# Revit family: Domotics-DomesticRanges-GEWISS-CHORUS_POWER-SOCKET-OUTLET_13A_ENG
name_source: partatom
category: Apparecchi elettrici
revit_build: Autodesk Revit 2016 (Build: 20161004_0715(x64)
units: mm (PartAtom-declared; Revit-internal decimal feet)

## family parameters
Condiviso = Sì
Host = Superficie
Mantenere orientamento annotazione = Sì
Punto di calcolo locali = Sì
Quota connettore circolare = Usa diametro
Taglio con vuoti quando caricato = Sì
Tipo di parte = Normale

## types (3) — shared parameters
Breaking capacity: = 1.25 In (100 position changes)
Carico apparente = 0 VA
Catalogue = DOMOTICS
Catalogue Range = CHORUS - DOMESTIC RANGE
Category = Socket-outlet
Characteristics = With safety shields
Description. = Socket-outlet
Description: = 2P+E - 13 A
Electrocod = 0131
For plug pins = Flat
Glow Wire Test = 850°C
IDF = 4440e827-df6d-472c-b9d9-53e8d2a5a7e6
IDT = 52e84893-02ac-4204-bcc4-ffe003daef48
Immagine tipo = GW14296.jpg
Insulation resistance = > 5 MOhm
N. poli = 1
No. Chorus modules = 2
No. Chorus modules: = 2
Produttore = GEWISS S.p.A.
Prolonged operation (no.of position changes) = 10.000 at In 250 V ac cosÃ˜=0,8
Prospetto di default = 1219 mm
Resistance at test voltage = 2000 V at 50 Hz for 1 minute
SEO = Socket outlet
Standard = UK
Standard: = British
Standard; = IEC 60884-1; BS 1363-2
TXT ELETTRICO = 13
Technical sheet = https://www.gewiss.com
Terminal grip on cable traction = > 50 N
Terminal tightening capacity flexible cables (mm2) = min. 0,75 - max. 2x4
Terminal tightening capacity rigid cables (mm2) = min. 0,5 - max. 2x2,5
Thermo-pressure with ball = 125
Tipo = Chorus Prese Eng 13A_GENERICO : GW14296 Presa 2M 2P+T 13A standard Inglese titanio
URL = https://www.gewiss.com
Version file RFA = 19.0
Volt = 230 V
Voltage = 250 V ac
Voltage: = 250 V ac
Wiring terminals = With screw

## per-type parameters (varying)
| type | Colour | Descrizione | EAN code | Modello |
| GW10296 - Socket outlet 2M 2P+E 13A uk white | White | S. OUTLET 2M 2P+E 13A UK WHITE | 8011564257986 | GW10296 |
| GW12296 - Socket outlet 2M 2P+E 13A uk standard black | Black | SOCKET 2M 2P+E 13A UK STANDARD BLACK | 8011564266957 | GW12296 |
| GW14296 - Socket outlet 2M 2P+E 13A uk standard titanium | Titanium | SOCKET 2M 2P+E 13A UK STANDARD TITANIUM | 8011564266438 | GW14296 |

note: source unit labels omitted for Thermo-pressure with ball — the stored unit's dimension contradicts the parameter name (converter mislabeling)

## geometry (parser evidence)
native form markers: Sweep x1
no freeform markers — native parametric forms only
